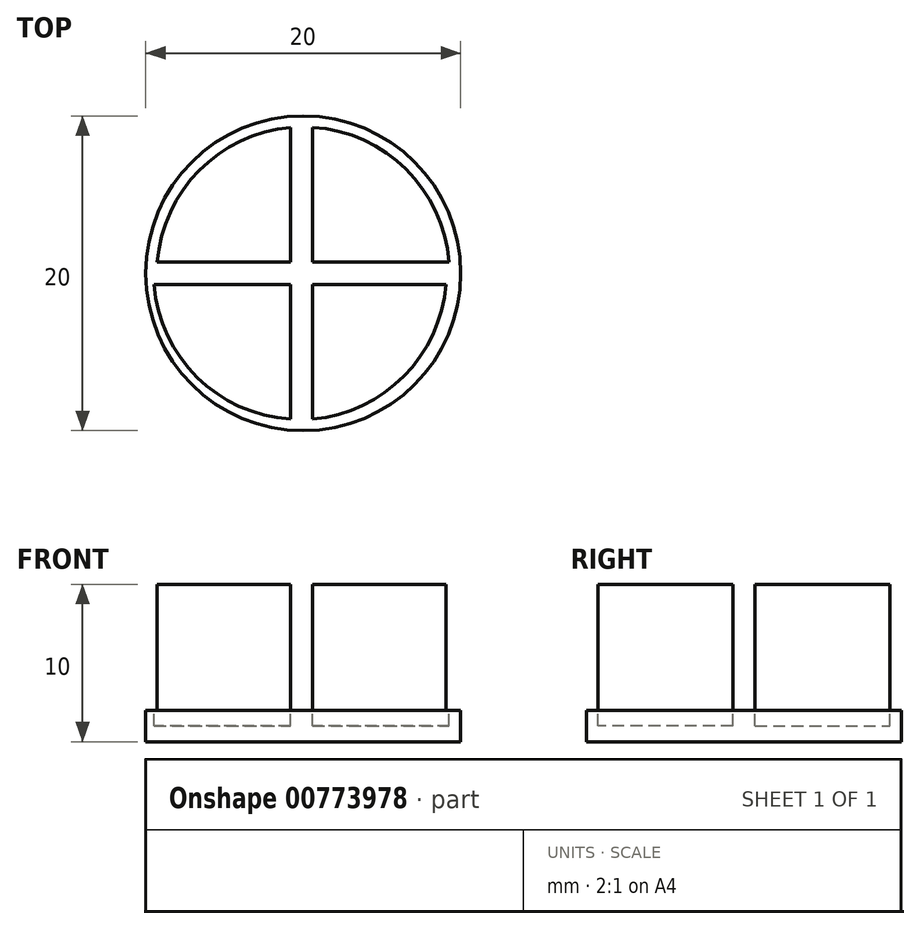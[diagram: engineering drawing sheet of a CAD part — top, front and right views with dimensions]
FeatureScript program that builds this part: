
annotation { "Feature Type Name" : "Feature", "Feature Type Description" : "" }
export const myFeature = defineFeature(function(context is Context, id is Id, definition is map)
    precondition{}
    {
        {
            var Q0;
            Q0=qCreatedBy(makeId("Top.planeOp"),FACE);
            var sketch = newSketch(context, id + "F0", { "sketchPlane" : qUnion([Q0])});
            skCircle(sketch, "E0", {"center": v(0.1, 0) * mm, "radius": 10 * mm});
            skSolve(sketch);
        }
        {
            var Q0;
            Q0 = qSketchRegion(id + "F0", true);
            extrude(context, id + "F1", {"entities" : qUnion([Q0]), "depth" : 2 * mm, "offsetDistance" : 25 * mm});
        }
        {
            var Q0;
            Q0=makeQuery(id+"F1.opExtrude","CAP_FACE",FACE,{"disambiguationData":[OSD([sQuery(id+"F0.wireOp",EDGE,"E0")])],"isStart":false});
            var sketch = newSketch(context, id + "F2", { "sketchPlane" : qUnion([Q0])});
            skLineSegment(sketch, "E1", {"start": v(0, 0) * mm, "end": v(-9.9, 0) * mm});
            skLineSegment(sketch, "E2", {"start": v(0, 0) * mm, "end": v(0, 10) * mm});
            skLineSegment(sketch, "E3", {"start": v(0, 0) * mm, "end": v(10.1, 0) * mm});
            skLineSegment(sketch, "E4", {"start": v(0, 0) * mm, "end": v(0, -10) * mm});
            skArc(sketch, "E5", {"start": v(0, 10) * mm, "mid": v(-7, 7.03) * mm, "end": v(-9.9, 0) * mm});
            skArc(sketch, "E6.0", {"start": v(-0.7, 9.26) * mm, "mid": v(-6.5, 6.53) * mm, "end": v(-9.17, 0.7) * mm});
            skLineSegment(sketch, "E6.1", {"start": v(-0.7, 0.7) * mm, "end": v(-0.7, 9.26) * mm});
            skLineSegment(sketch, "E6.2", {"start": v(-0.7, 0.7) * mm, "end": v(-9.17, 0.7) * mm});
            skArc(sketch, "E7.1.0", {"start": v(0.7, -9.26) * mm, "mid": v(6.5, -6.53) * mm, "end": v(9.17, -0.7) * mm});
            skLineSegment(sketch, "E7.1.1", {"start": v(0.7, -0.7) * mm, "end": v(0.7, -9.26) * mm});
            skLineSegment(sketch, "E7.1.2", {"start": v(0.7, -0.7) * mm, "end": v(9.17, -0.7) * mm});
            skPoint(sketch, "E7.center", {"position": v(0, 0) * mm});
            skArc(sketch, "E8", {"start": v(10.1, 0) * mm, "mid": v(7.14, 7.1) * mm, "end": v(0, 10) * mm});
            skArc(sketch, "E9.0", {"start": v(9.37, 0.71) * mm, "mid": v(6.64, 6.6) * mm, "end": v(0.71, 9.27) * mm});
            skLineSegment(sketch, "E9.1", {"start": v(0.71, 0.71) * mm, "end": v(9.37, 0.71) * mm});
            skLineSegment(sketch, "E9.2", {"start": v(0.71, 0.71) * mm, "end": v(0.71, 9.27) * mm});
            skArc(sketch, "E10.1.0", {"start": v(-9.37, -0.71) * mm, "mid": v(-6.64, -6.6) * mm, "end": v(-0.71, -9.27) * mm});
            skLineSegment(sketch, "E10.1.1", {"start": v(-0.71, -0.71) * mm, "end": v(-0.71, -9.27) * mm});
            skLineSegment(sketch, "E10.1.2", {"start": v(-0.71, -0.71) * mm, "end": v(-9.37, -0.71) * mm});
            skSolve(sketch);
        }
        {
            var Q0;
            Q0=makeQuery(id+"F2.imprint","IMPRINT",FACE,{"disambiguationData":[TD([[makeQuery(id+"F2.imprint","IMPRINT",EDGE,{"derivedFrom":sQuery(id+"F2.wireOp",EDGE,"E7.1.0")}),1.0]])]});
            var Q1;
            Q1=makeQuery(id+"F2.imprint","IMPRINT",FACE,{"disambiguationData":[TD([[makeQuery(id+"F2.imprint","IMPRINT",EDGE,{"derivedFrom":sQuery(id+"F2.wireOp",EDGE,"E6.0")}),1.0]])]});
            extrude(context, id + "F3", {"entities" : qUnion([Q0, Q1]), "operationType" : NewBodyOperationType.ADD, "depth" : 8 * mm, "offsetDistance" : 25 * mm});
        }
        {
            var Q0;
            Q0=makeQuery(id+"F2.imprint","IMPRINT",FACE,{"disambiguationData":[TD([[makeQuery(id+"F2.imprint","IMPRINT",EDGE,{"derivedFrom":sQuery(id+"F2.wireOp",EDGE,"E9.0")}),1.0]])]});
            var Q1;
            Q1=makeQuery(id+"F2.imprint","IMPRINT",FACE,{"disambiguationData":[TD([[makeQuery(id+"F2.imprint","IMPRINT",EDGE,{"derivedFrom":sQuery(id+"F2.wireOp",EDGE,"E10.1.0")}),1.0]])]});
            extrude(context, id + "F4", {"entities" : qUnion([Q0, Q1]), "operationType" : NewBodyOperationType.REMOVE, "oppositeDirection" : true, "depth" : 1 * mm, "offsetDistance" : 25 * mm});
        }
    });
